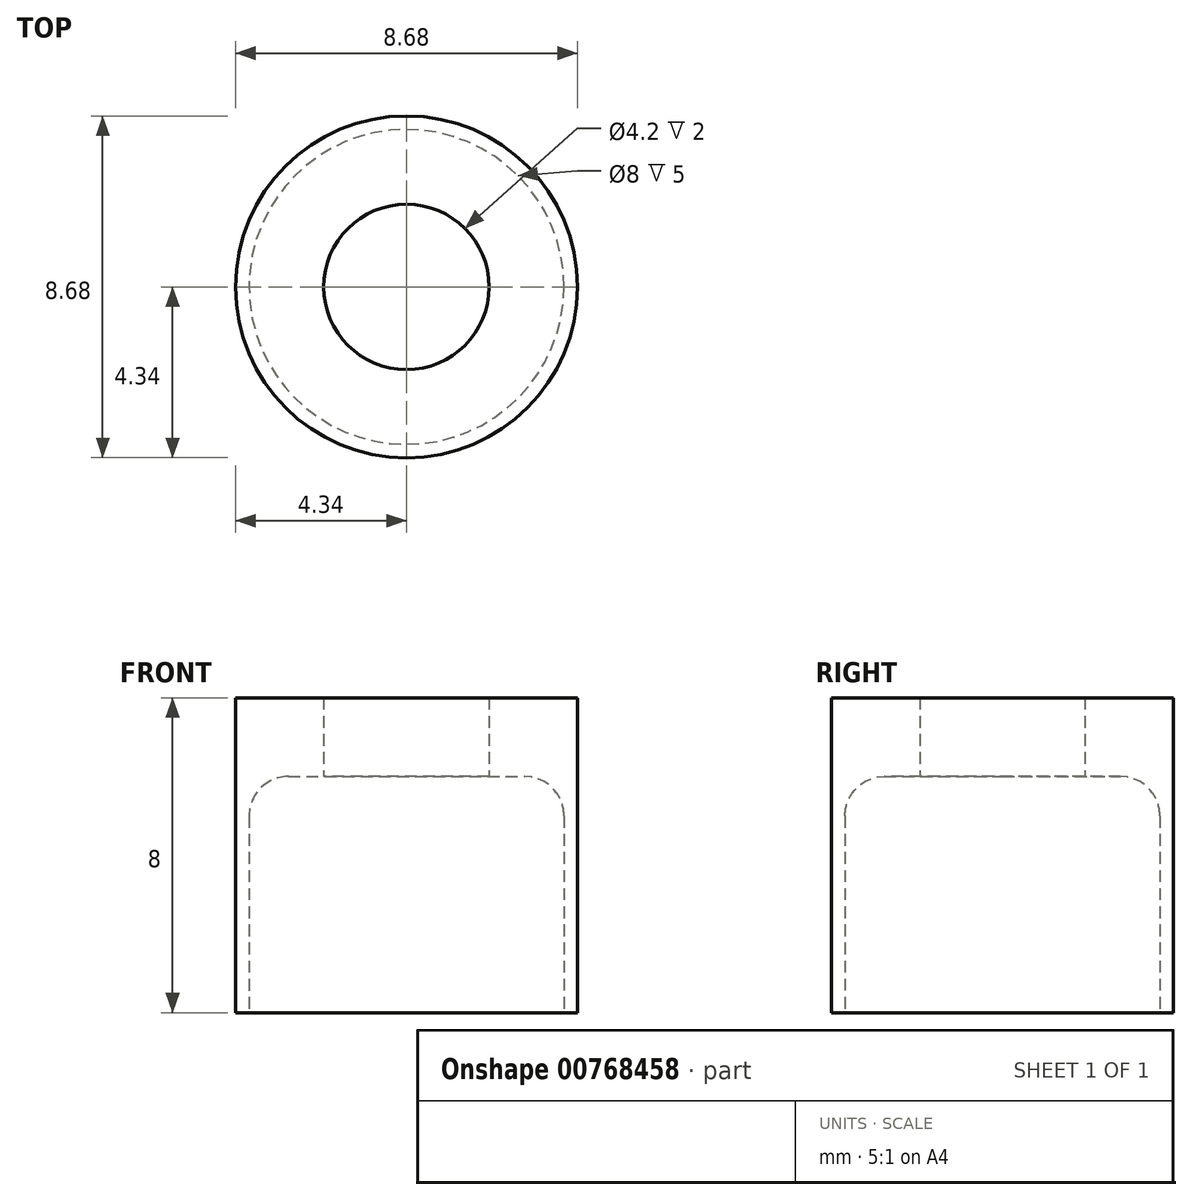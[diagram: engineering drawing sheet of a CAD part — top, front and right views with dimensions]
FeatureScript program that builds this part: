
annotation { "Feature Type Name" : "Feature", "Feature Type Description" : "" }
export const myFeature = defineFeature(function(context is Context, id is Id, definition is map)
    precondition{}
    {
        {
            var Q0;
            Q0=qCreatedBy(makeId("Top.planeOp"),FACE);
            var sketch = newSketch(context, id + "F0", { "sketchPlane" : qUnion([Q0])});
            skCircle(sketch, "E0", {"center": v(0, 0) * mm, "radius": 2.1 * mm});
            skCircle(sketch, "E1", {"center": v(0, 0) * mm, "radius": 3.5 * mm});
            skLineSegment(sketch, "E2.bottom", {"start": v(4.5, 4.5) * mm, "end": v(-4.5, 4.5) * mm});
            skLineSegment(sketch, "E2.top", {"start": v(4.5, -4.5) * mm, "end": v(-4.5, -4.5) * mm});
            skLineSegment(sketch, "E2.left", {"start": v(4.5, 4.5) * mm, "end": v(4.5, -4.5) * mm});
            skLineSegment(sketch, "E2.right", {"start": v(-4.5, 4.5) * mm, "end": v(-4.5, -4.5) * mm});
            skSolve(sketch);
        }
        {
            var Q0;
            Q0=makeQuery(id+"F0.imprint","IMPRINT",FACE,{"disambiguationData":[TD([[makeQuery(id+"F0.imprint","IMPRINT",EDGE,{"derivedFrom":sQuery(id+"F0.wireOp",EDGE,"E0")}),-1.0]])]});
            var Q1;
            Q1=makeQuery(id+"F0.imprint","IMPRINT",FACE,{"disambiguationData":[TD([[makeQuery(id+"F0.imprint","IMPRINT",EDGE,{"derivedFrom":sQuery(id+"F0.wireOp",EDGE,"E1")}),-1.0]])]});
            extrude(context, id + "F1", {"entities" : qUnion([Q0, Q1]), "depth" : 8 * mm, "offsetDistance" : 25 * mm});
        }
        {
            var Q0;
            Q0=makeQuery(id+"F1.opExtrude","CAP_FACE",FACE,{"disambiguationData":[OSD([sQuery(id+"F0.wireOp",EDGE,"E0"),sQuery(id+"F0.wireOp",EDGE,"E2.bottom"),sQuery(id+"F0.wireOp",EDGE,"E2.top"),sQuery(id+"F0.wireOp",EDGE,"E2.left"),sQuery(id+"F0.wireOp",EDGE,"E2.right")])],"isStart":true});
            var sketch = newSketch(context, id + "F2", { "sketchPlane" : qUnion([Q0])});
            skCircle(sketch, "E3", {"center": v(0, 0) * mm, "radius": 4 * mm});
            skSolve(sketch);
        }
        {
            var Q0;
            Q0=makeQuery(id+"F2.imprint","IMPRINT",FACE,{"disambiguationData":[TD([[makeQuery(id+"F2.imprint","IMPRINT",EDGE,{"derivedFrom":sQuery(id+"F2.wireOp",EDGE,"E3")}),1.0]])]});
            extrude(context, id + "F3", {"entities" : qUnion([Q0]), "operationType" : NewBodyOperationType.REMOVE, "oppositeDirection" : true, "depth" : 6 * mm, "offsetDistance" : 25 * mm});
        }
        {
            var Q0;
            Q0=makeQuery(id+"F3.boolean.opBoolean","COPY",EDGE,{"derivedFrom":makeQuery(id+"F3.opExtrude","CAP_EDGE",EDGE,{"disambiguationData":[OSD([sQuery(id+"F2.wireOp",EDGE,"E3")])],"isStart":false})});
            fillet(context, id + "F4", {"entities" : qUnion([Q0]), "radius" : 1 * mm, "tangentPropagation" : true, "allowEdgeOverflow" : false});
        }
        {
            var Q0;
            Q0=makeQuery(id+"F1.opExtrude","CAP_FACE",FACE,{"disambiguationData":[OSD([sQuery(id+"F0.wireOp",EDGE,"E0"),sQuery(id+"F0.wireOp",EDGE,"E2.bottom"),sQuery(id+"F0.wireOp",EDGE,"E2.top"),sQuery(id+"F0.wireOp",EDGE,"E2.left"),sQuery(id+"F0.wireOp",EDGE,"E2.right")])],"isStart":true});
            var sketch = newSketch(context, id + "F5", { "sketchPlane" : qUnion([Q0])});
            skCircle(sketch, "E4", {"center": v(0, 0) * mm, "radius": 4.34 * mm});
            skCircle(sketch, "E5", {"center": v(0, 0) * mm, "radius": 7 * mm});
            skSolve(sketch);
        }
        {
            var Q0;
            Q0 = qSketchRegion(id + "F5", true);
            extrude(context, id + "F6", {"entities" : qUnion([Q0]), "operationType" : NewBodyOperationType.REMOVE, "oppositeDirection" : true, "depth" : 25 * mm, "offsetDistance" : 25 * mm});
        }
    });
